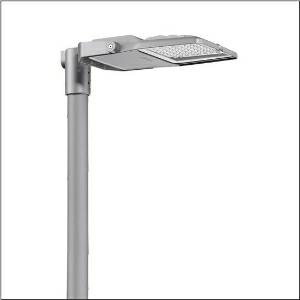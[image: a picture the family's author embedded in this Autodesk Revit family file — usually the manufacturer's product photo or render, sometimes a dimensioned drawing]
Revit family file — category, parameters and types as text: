
# Revit family: floodlight_fl_21_mini___pl61_5xa7775c2c3a_8aba
name_source: partatom
category: Lighting Fixtures
units: mm (PartAtom-declared; Revit-internal decimal feet)

## family parameters
Cut with Voids When Loaded = No
Host = Face
Light Source = No
Part Type = Normal
Room Calculation Point = No
Round Connector Dimension = Use Diameter
Shared = No

## types (1)
- --- (1 x LED, 11960 lm, 89 W, 3000K)
    Apparent Load = 89 VA
    CIE Flux Codes = 33 65 98 100 100
    Color Rendering = 70
    Color Temperature = 3000K
    Default Elevation = 1800 mm
    Description = Floodlight FL 21 mini, floodlight, primary light control with lens, of PMMA, primary optical cover: protective disc, of toughened safety glass, transparent, light distribution: PL61, light emission: direct distribution, installation type: surface-mounted, LED, High Power LED, rated luminous flux: 11.960lm, luminous efficacy: 134lm/W, light colour: 730, colour temperature: 3000K, control gear: Smart Interface (Zhaga), control: flexible luminous flux parameterisation, time-dependent luminous flux control, constant luminous flux control, overheat protection, pre-setting: logarithmic dimming characteristic, with terminal, 6-pole, mains connection: 220..240V, AC, 50/60Hz, start of lifetime: 89W, end of service life: 94W, reduction: 43W, luminaire housing, of diecast aluminium, powder-coated, SITECO metallic grey (DB 702S), corrosivity category C5 mid according to DIN EN ISO 12944, suitable for swimming pools, chlorine-resistant, sealing non-destructively replaceable, please order mast flange separately, mast bracket, of steel, galvanised, powder-coated, SITECO metallic grey (DB 702S), Smart Interface above, protection rating (complete): IP66, insulation class (complete): insulation class II (safety insulation), certification: CE, ENEC, VDE, protection symbol: D, impact resistance: IK08, permissible operating ambient temperature: -40..+40°C, permissible operating ambient temperature for outdoor applications: -40..+50°C, standard: DIN EN 12944, LABS conformity tested according to VDMA 24364:2018-05, packaging unit: 1 piece

Light Distribution: PL61
    Height = 70 mm
    Lamp = 1 x LED
    Lamp Light Flux = 11960 lm
    Lamp Power = 89 W
    Lamp count = 1
    Length = 485 mm
    Luminous efficacy = 134 lm/W
    Manufacturer = Siteco
    ModVariant = No
    Model = 5XA7775C2C3A
    Number of Poles = 1
    OnlyDefault = Yes
    Power Factor = 1
    Product Name = Floodlight FL 21 mini | PL61
    Product group = floodlight | pylon annexe
    ProductGroupID = 6201
    Protection Class = Protection class II
    Protection Degree = IP 66
    RLX_Detail_Level = 1
    RLX_Emergency_Light_Flux = 0 lm
    RLX_Emergency_Type = 0
    RLX_Emergency_Type_DB = No
    RlxData = <blob elided: 100989 chars, md5=960d4b1a>
    Socket = socket
    Standby Power = 0 W
    System Light Flux = 11960 lm
    System Power = 89 W
    Type Comments = factory setting: luminous flux: 100 % | dim-lin: 254 | 456 mA
    Type Image = l_1007125.jpg
    URL = http://relux.com
    VarID = @adj_171543
    Voltage = 0 V
    Weight = 0.00 kg
    Width = 337 mm

## geometry (parser evidence)
native form markers: Blend x4, Sweep x14
no freeform markers — native parametric forms only
